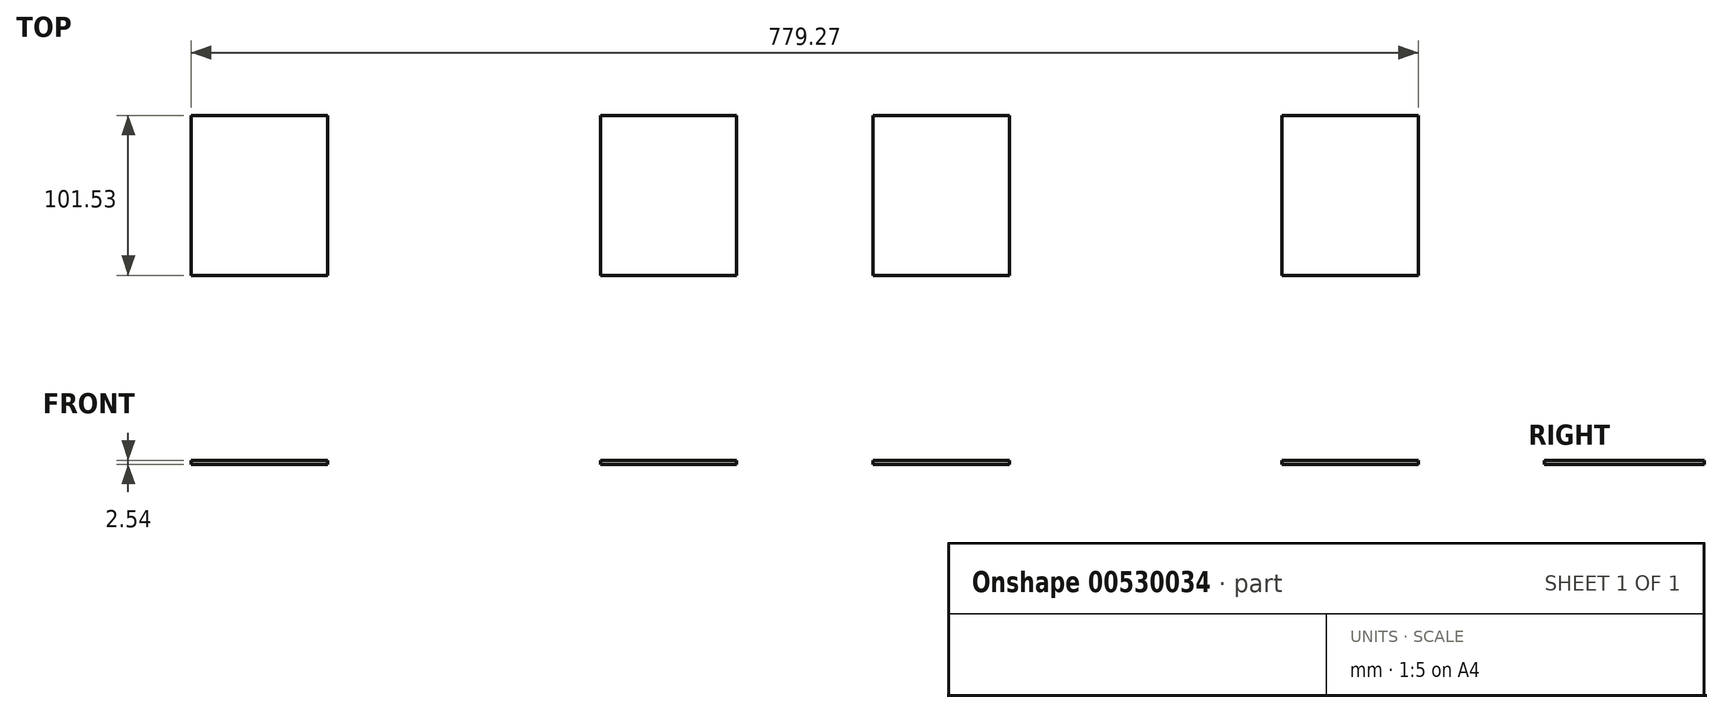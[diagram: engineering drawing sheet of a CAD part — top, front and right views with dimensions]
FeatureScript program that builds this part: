
annotation { "Feature Type Name" : "Feature", "Feature Type Description" : "" }
export const myFeature = defineFeature(function(context is Context, id is Id, definition is map)
    precondition{}
    {
        {
            var Q0;
            Q0=qCreatedBy(makeId("Top.planeOp"),FACE);
            var sketch = newSketch(context, id + "F0", { "sketchPlane" : qUnion([Q0])});
            skLineSegment(sketch, "E0.left", {"start": v(-74.8, 56.96) * mm, "end": v(-74.8, -44.57) * mm});
            skLineSegment(sketch, "E0.right", {"start": v(11.79, 56.96) * mm, "end": v(11.79, -44.57) * mm});
            skLineSegment(sketch, "E1.bottom", {"start": v(11.79, 56.96) * mm, "end": v(98.37, 56.96) * mm});
            skLineSegment(sketch, "E1.top", {"start": v(11.79, -44.57) * mm, "end": v(98.37, -44.57) * mm});
            skLineSegment(sketch, "E2", {"start": v(98.37, 56.96) * mm, "end": v(98.37, -44.57) * mm});
            skLineSegment(sketch, "E3.MirrorCS", {"start": v(-74.8, -44.57) * mm, "end": v(-161.38, -44.57) * mm});
            skLineSegment(sketch, "E4.MirrorCS", {"start": v(-74.8, 56.96) * mm, "end": v(-161.38, 56.96) * mm});
            skLineSegment(sketch, "E5.MirrorCS", {"start": v(-161.38, 56.96) * mm, "end": v(-161.38, -44.57) * mm});
            skLineSegment(sketch, "E6.MirrorCS", {"start": v(358.13, -44.57) * mm, "end": v(271.55, -44.57) * mm});
            skLineSegment(sketch, "E7.MirrorCS", {"start": v(358.13, 56.96) * mm, "end": v(358.13, -44.57) * mm});
            skLineSegment(sketch, "E8.MirrorCS", {"start": v(271.55, 56.96) * mm, "end": v(271.55, -44.57) * mm});
            skLineSegment(sketch, "E9.MirrorCS", {"start": v(358.13, 56.96) * mm, "end": v(271.55, 56.96) * mm});
            skLineSegment(sketch, "E10.MirrorCS", {"start": v(-421.14, -44.57) * mm, "end": v(-334.56, -44.57) * mm});
            skLineSegment(sketch, "E11.MirrorCS", {"start": v(-421.14, 56.96) * mm, "end": v(-421.14, -44.57) * mm});
            skLineSegment(sketch, "E12.MirrorCS", {"start": v(-334.56, 56.96) * mm, "end": v(-334.56, -44.57) * mm});
            skLineSegment(sketch, "E13.MirrorCS", {"start": v(-421.14, 56.96) * mm, "end": v(-334.56, 56.96) * mm});
            skSolve(sketch);
        }
        {
            var Q0;
            Q0=makeQuery(id+"F0.imprint","IMPRINT",FACE,{"disambiguationData":[TD([[makeQuery(id+"F0.imprint","IMPRINT",EDGE,{"derivedFrom":sQuery(id+"F0.wireOp",EDGE,"E10.MirrorCS")}),1.0]])]});
            extrude(context, id + "F1", {"entities" : qUnion([Q0]), "depth" : 2.54 * mm, "offsetDistance" : 25.4 * mm});
        }
        {
            var Q0;
            Q0=makeQuery(id+"F0.imprint","IMPRINT",FACE,{"disambiguationData":[TD([[makeQuery(id+"F0.imprint","IMPRINT",EDGE,{"derivedFrom":sQuery(id+"F0.wireOp",EDGE,"E0.left")}),-1.0]])]});
            extrude(context, id + "F2", {"entities" : qUnion([Q0]), "depth" : 2.54 * mm, "offsetDistance" : 25.4 * mm});
        }
        {
            var Q0;
            Q0=makeQuery(id+"F0.imprint","IMPRINT",FACE,{"disambiguationData":[TD([[makeQuery(id+"F0.imprint","IMPRINT",EDGE,{"derivedFrom":sQuery(id+"F0.wireOp",EDGE,"E1.bottom")}),-1.0]])]});
            extrude(context, id + "F3", {"entities" : qUnion([Q0]), "depth" : 2.54 * mm, "offsetDistance" : 25.4 * mm});
        }
        {
            var Q0;
            Q0=makeQuery(id+"F0.imprint","IMPRINT",FACE,{"disambiguationData":[TD([[makeQuery(id+"F0.imprint","IMPRINT",EDGE,{"derivedFrom":sQuery(id+"F0.wireOp",EDGE,"E6.MirrorCS")}),-1.0]])]});
            extrude(context, id + "F4", {"entities" : qUnion([Q0]), "depth" : 2.54 * mm, "offsetDistance" : 25.4 * mm});
        }
    });
